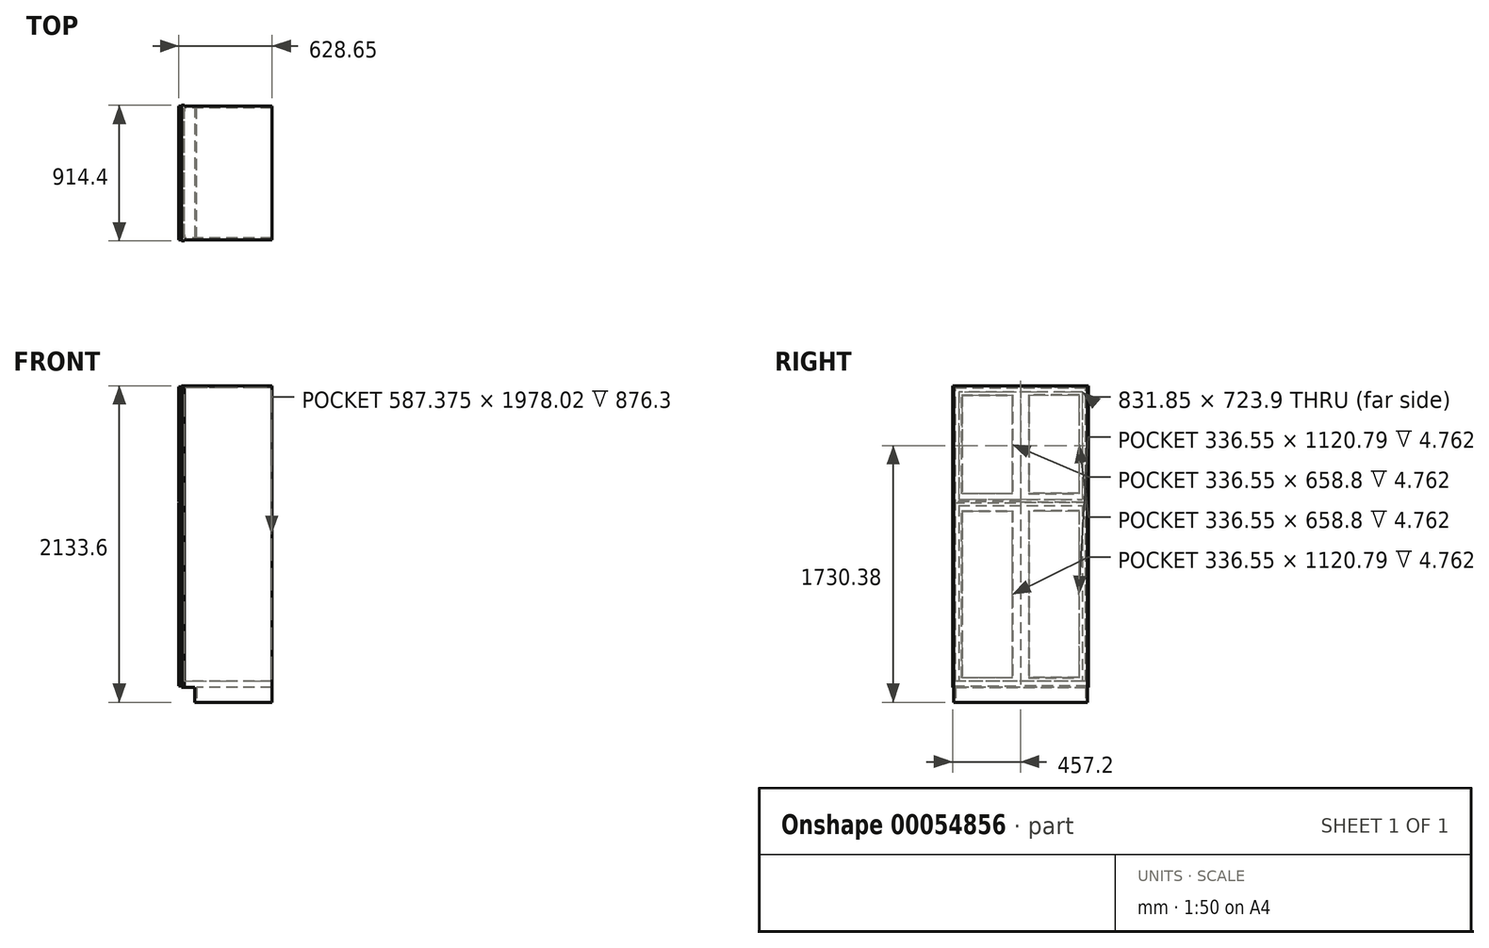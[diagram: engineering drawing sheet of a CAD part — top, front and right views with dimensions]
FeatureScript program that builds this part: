
annotation { "Feature Type Name" : "Feature", "Feature Type Description" : "" }
export const myFeature = defineFeature(function(context is Context, id is Id, definition is map)
    precondition{}
    {
        {
            var Q0;
            Q0=qCreatedBy(makeId("Front.planeOp"),FACE);
            var sketch = newSketch(context, id + "F0", { "sketchPlane" : qUnion([Q0])});
            skLineSegment(sketch, "E0.bottom", {"start": v(-304.8, -1066.8) * mm, "end": v(304.8, -1066.8) * mm});
            skLineSegment(sketch, "E0.top", {"start": v(-304.8, 1066.8) * mm, "end": v(304.8, 1066.8) * mm});
            skLineSegment(sketch, "E0.left", {"start": v(-304.8, -1066.8) * mm, "end": v(-304.8, 1066.8) * mm});
            skLineSegment(sketch, "E0.right", {"start": v(304.8, -1066.8) * mm, "end": v(304.8, 1066.8) * mm});
            skLineSegment(sketch, "E1", {"start": v(-304.8, -1066.8) * mm, "end": v(304.8, 1066.8) * mm, "construction": true});
            skSolve(sketch);
        }
        {
            var Q0;
            Q0=qSketchRegion(id+"F0",true);
            extrude(context, id + "F1", {"entities" : qUnion([Q0]), "oppositeDirection" : true, "depth" : 914.4 * mm});
        }
        {
            var Q0;
            Q0=makeQuery(id+"F1.opExtrude","CAP_FACE",FACE,{"disambiguationData":[OSD([sQuery(id+"F0.wireOp",EDGE,"E0.bottom"),sQuery(id+"F0.wireOp",EDGE,"E0.top"),sQuery(id+"F0.wireOp",EDGE,"E0.left"),sQuery(id+"F0.wireOp",EDGE,"E0.right")])],"isStart":true});
            var sketch = newSketch(context, id + "F2", { "sketchPlane" : qUnion([Q0])});
            skLineSegment(sketch, "E2.bottom", {"start": v(-304.8, -1066.8) * mm, "end": v(-215.9, -1066.8) * mm});
            skLineSegment(sketch, "E2.top", {"start": v(-304.8, -965.2) * mm, "end": v(-215.9, -965.2) * mm});
            skLineSegment(sketch, "E2.left", {"start": v(-304.8, -1066.8) * mm, "end": v(-304.8, -965.2) * mm});
            skLineSegment(sketch, "E2.right", {"start": v(-215.9, -1066.8) * mm, "end": v(-215.9, -965.2) * mm});
            skSolve(sketch);
        }
        {
            var Q0;
            Q0=qSketchRegion(id+"F2",true);
            extrude(context, id + "F3", {"entities" : qUnion([Q0]), "operationType" : NewBodyOperationType.REMOVE, "endBound" : BoundingType.THROUGH_ALL, "oppositeDirection" : true, "depth" : 25.4 * mm});
        }
        {
            var Q0;
            Q0=makeQuery(id+"F1.opExtrude","SWEPT_FACE",FACE,{"disambiguationData":[OSD([sQuery(id+"F0.wireOp",EDGE,"E0.left")])]});
            var sketch = newSketch(context, id + "F4", { "sketchPlane" : qUnion([Q0])});
            skLineSegment(sketch, "E3.bottom", {"start": v(-873.13, 1025.53) * mm, "end": v(-41.28, 1025.53) * mm});
            skLineSegment(sketch, "E3.top", {"start": v(-873.12, -923.93) * mm, "end": v(-41.27, -923.93) * mm});
            skLineSegment(sketch, "E3.left", {"start": v(-873.13, 1025.53) * mm, "end": v(-873.12, -923.93) * mm});
            skLineSegment(sketch, "E3.right", {"start": v(-41.28, 1025.53) * mm, "end": v(-41.27, -923.93) * mm});
            skSolve(sketch);
        }
        {
            var Q0;
            Q0=qSketchRegion(id+"F4",true);
            extrude(context, id + "F5", {"entities" : qUnion([Q0]), "operationType" : NewBodyOperationType.REMOVE, "oppositeDirection" : true, "depth" : 19.05 * mm});
        }
        {
            var Q0;
            Q0=makeQuery(id+"F1.opExtrude","SWEPT_FACE",FACE,{"disambiguationData":[OSD([sQuery(id+"F0.wireOp",EDGE,"E0.top")])]});
            var sketch = newSketch(context, id + "F6", { "sketchPlane" : qUnion([Q0])});
            skLineSegment(sketch, "E4.bottom", {"start": v(304.8, 914.4) * mm, "end": v(-285.75, 914.4) * mm});
            skLineSegment(sketch, "E4.top", {"start": v(304.8, 908.05) * mm, "end": v(-285.75, 908.05) * mm});
            skLineSegment(sketch, "E4.left", {"start": v(304.8, 914.4) * mm, "end": v(304.8, 908.05) * mm});
            skLineSegment(sketch, "E4.right", {"start": v(-285.75, 914.4) * mm, "end": v(-285.75, 908.05) * mm});
            skLineSegment(sketch, "E5.bottom", {"start": v(304.8, 0) * mm, "end": v(-285.75, 0) * mm});
            skLineSegment(sketch, "E5.top", {"start": v(304.8, 6.35) * mm, "end": v(-285.75, 6.35) * mm});
            skLineSegment(sketch, "E5.left", {"start": v(304.8, 0) * mm, "end": v(304.8, 6.35) * mm});
            skLineSegment(sketch, "E5.right", {"start": v(-285.75, 0) * mm, "end": v(-285.75, 6.35) * mm});
            skSolve(sketch);
        }
        {
            var Q0;
            Q0=qSketchRegion(id+"F6",true);
            extrude(context, id + "F7", {"entities" : qUnion([Q0]), "operationType" : NewBodyOperationType.REMOVE, "endBound" : BoundingType.THROUGH_ALL, "oppositeDirection" : true, "depth" : 25.4 * mm});
        }
        {
            var Q0;
            Q0=makeQuery(id+"F1.opExtrude","SWEPT_FACE",FACE,{"disambiguationData":[OSD([sQuery(id+"F0.wireOp",EDGE,"E0.top")])]});
            var sketch = newSketch(context, id + "F8", { "sketchPlane" : qUnion([Q0])});
            skLineSegment(sketch, "E6.bottom", {"start": v(301.63, 895.35) * mm, "end": v(-285.75, 895.35) * mm});
            skLineSegment(sketch, "E6.top", {"start": v(301.63, 19.05) * mm, "end": v(-285.75, 19.05) * mm});
            skLineSegment(sketch, "E6.left", {"start": v(301.62, 895.35) * mm, "end": v(301.63, 19.05) * mm});
            skLineSegment(sketch, "E6.right", {"start": v(-285.75, 895.35) * mm, "end": v(-285.75, 19.05) * mm});
            skSolve(sketch);
        }
        {
            var Q0;
            Q0=qSketchRegion(id+"F8",true);
            var Q1;
            Q1=makeQuery(id+"F5.boolean.opBoolean","COPY",FACE,{"derivedFrom":makeQuery(id+"F5.opExtrude","SWEPT_FACE",FACE,{"disambiguationData":[OSD([sQuery(id+"F4.wireOp",EDGE,"E3.top")])]})});
            extrude(context, id + "F9", {"entities" : qUnion([Q0]), "operationType" : NewBodyOperationType.REMOVE, "endBound" : BoundingType.UP_TO_SURFACE, "oppositeDirection" : true, "endBoundEntityFace" : qUnion([Q1]), "depth" : 25.4 * mm});
        }
        {
            var Q0;
            Q0=makeQuery(id+"F1.opExtrude","SWEPT_FACE",FACE,{"disambiguationData":[OSD([sQuery(id+"F0.wireOp",EDGE,"E0.left")])]});
            var sketch = newSketch(context, id + "F10", { "sketchPlane" : qUnion([Q0])});
            skLineSegment(sketch, "E7.bottom", {"start": v(-873.13, 301.63) * mm, "end": v(-41.28, 301.63) * mm});
            skLineSegment(sketch, "E7.top", {"start": v(-873.13, 260.35) * mm, "end": v(-41.28, 260.35) * mm});
            skLineSegment(sketch, "E7.left", {"start": v(-873.13, 301.63) * mm, "end": v(-873.13, 260.35) * mm});
            skLineSegment(sketch, "E7.right", {"start": v(-41.28, 301.63) * mm, "end": v(-41.28, 260.35) * mm});
            skSolve(sketch);
        }
        {
            var Q0;
            Q0=qSketchRegion(id+"F10",true);
            var Q1;
            Q1=makeQuery(id+"F9.boolean.opBoolean","COPY",FACE,{"derivedFrom":makeQuery(id+"F9.opExtrude","SWEPT_FACE",FACE,{"disambiguationData":[OSD([sQuery(id+"F8.wireOp",EDGE,"E6.right")])]})});
            extrude(context, id + "F11", {"entities" : qUnion([Q0]), "operationType" : NewBodyOperationType.ADD, "endBound" : BoundingType.UP_TO_SURFACE, "oppositeDirection" : true, "endBoundEntityFace" : qUnion([Q1]), "depth" : 25.4 * mm});
        }
        {
            var Q0;
            Q0=makeQuery(id+"F11.boolean.opBoolean","MERGE",FACE,{"derivedFrom":[makeQuery(id+"F1.opExtrude","SWEPT_FACE",FACE,{"disambiguationData":[OSD([sQuery(id+"F0.wireOp",EDGE,"E0.left")])]}),makeQuery(id+"F11.opExtrude","CAP_FACE",FACE,{"disambiguationData":[OSD([sQuery(id+"F10.wireOp",EDGE,"E7.bottom"),sQuery(id+"F10.wireOp",EDGE,"E7.top"),sQuery(id+"F10.wireOp",EDGE,"E7.left"),sQuery(id+"F10.wireOp",EDGE,"E7.right")])],"isStart":true})]});
            var sketch = newSketch(context, id + "F12", { "sketchPlane" : qUnion([Q0])});
            skLineSegment(sketch, "E8.bottom", {"start": v(-908.05, 277.83) * mm, "end": v(-457.2, 277.83) * mm});
            skLineSegment(sketch, "E8.top", {"start": v(-908.05, -957.26) * mm, "end": v(-457.2, -957.26) * mm});
            skLineSegment(sketch, "E8.left", {"start": v(-908.05, 277.83) * mm, "end": v(-908.05, -957.26) * mm});
            skLineSegment(sketch, "E8.right", {"start": v(-457.2, 277.83) * mm, "end": v(-457.2, -957.26) * mm});
            skLineSegment(sketch, "E9.bottom", {"start": v(-850.9, 220.68) * mm, "end": v(-514.35, 220.68) * mm});
            skLineSegment(sketch, "E9.top", {"start": v(-850.9, -900.11) * mm, "end": v(-514.35, -900.11) * mm});
            skLineSegment(sketch, "E9.left", {"start": v(-850.9, 220.68) * mm, "end": v(-850.9, -900.11) * mm});
            skLineSegment(sketch, "E9.right", {"start": v(-514.35, 220.68) * mm, "end": v(-514.35, -900.11) * mm});
            skLineSegment(sketch, "E10", {"start": v(-457.2, 260.35) * mm, "end": v(-457.2, -923.93) * mm, "construction": true});
            skLineSegment(sketch, "E11.bottom", {"start": v(-457.2, 1058.86) * mm, "end": v(-908.05, 1058.86) * mm});
            skLineSegment(sketch, "E11.top", {"start": v(-457.2, 285.76) * mm, "end": v(-908.05, 285.76) * mm});
            skLineSegment(sketch, "E11.left", {"start": v(-457.2, 1058.86) * mm, "end": v(-457.2, 285.76) * mm});
            skLineSegment(sketch, "E11.right", {"start": v(-908.05, 1058.86) * mm, "end": v(-908.05, 285.76) * mm});
            skLineSegment(sketch, "E12.bottom", {"start": v(-850.9, 1001.71) * mm, "end": v(-514.35, 1001.71) * mm});
            skLineSegment(sketch, "E12.top", {"start": v(-850.9, 342.91) * mm, "end": v(-514.35, 342.91) * mm});
            skLineSegment(sketch, "E12.left", {"start": v(-850.9, 1001.71) * mm, "end": v(-850.9, 342.91) * mm});
            skLineSegment(sketch, "E12.right", {"start": v(-514.35, 1001.71) * mm, "end": v(-514.35, 342.91) * mm});
            skSolve(sketch);
        }
        {
            var Q0;
            Q0=qSketchRegion(id+"F12",true);
            extrude(context, id + "F13", {"entities" : qUnion([Q0]), "depth" : 19.05 * mm});
        }
        {
            var Q0;
            Q0=makeQuery(id+"F13.opExtrude","SWEPT_FACE",FACE,{"disambiguationData":[OSD([sQuery(id+"F12.wireOp",EDGE,"E9.top")])]});
            var sketch = newSketch(context, id + "F14", { "sketchPlane" : qUnion([Q0])});
            skLineSegment(sketch, "E13.bottom", {"start": v(-315.91, 850.9) * mm, "end": v(-309.56, 850.9) * mm});
            skLineSegment(sketch, "E13.top", {"start": v(-315.91, 514.35) * mm, "end": v(-309.56, 514.35) * mm});
            skLineSegment(sketch, "E13.left", {"start": v(-315.91, 850.9) * mm, "end": v(-315.91, 514.35) * mm});
            skLineSegment(sketch, "E13.right", {"start": v(-309.56, 850.9) * mm, "end": v(-309.56, 514.35) * mm});
            skSolve(sketch);
        }
        {
            var Q0;
            Q0=qSketchRegion(id+"F14",true);
            extrude(context, id + "F15", {"entities" : qUnion([Q0]), "operationType" : NewBodyOperationType.ADD, "endBound" : BoundingType.UP_TO_NEXT, "depth" : 25.4 * mm});
        }
        {
            var Q0;
            Q0=makeQuery(id+"F13.opExtrude","SWEPT_FACE",FACE,{"disambiguationData":[OSD([sQuery(id+"F12.wireOp",EDGE,"E12.top")])]});
            var sketch = newSketch(context, id + "F16", { "sketchPlane" : qUnion([Q0])});
            skLineSegment(sketch, "E14.bottom", {"start": v(-309.56, 850.9) * mm, "end": v(-315.91, 850.9) * mm});
            skLineSegment(sketch, "E14.top", {"start": v(-309.56, 514.35) * mm, "end": v(-315.91, 514.35) * mm});
            skLineSegment(sketch, "E14.left", {"start": v(-309.56, 850.9) * mm, "end": v(-309.56, 514.35) * mm});
            skLineSegment(sketch, "E14.right", {"start": v(-315.91, 850.9) * mm, "end": v(-315.91, 514.35) * mm});
            skSolve(sketch);
        }
        {
            var Q0;
            Q0=qSketchRegion(id+"F16",true);
            extrude(context, id + "F17", {"entities" : qUnion([Q0]), "operationType" : NewBodyOperationType.ADD, "endBound" : BoundingType.UP_TO_NEXT, "depth" : 25.4 * mm});
        }
        {
            var Q0;
            Q0=makeQuery(id+"F13.opExtrude","CAP_EDGE",EDGE,{"disambiguationData":[OSD([sQuery(id+"F12.wireOp",EDGE,"E9.left")])],"isStart":false});
            var Q1;
            Q1=makeQuery(id+"F13.opExtrude","CAP_EDGE",EDGE,{"disambiguationData":[OSD([sQuery(id+"F12.wireOp",EDGE,"E9.top")])],"isStart":false});
            var Q2;
            Q2=makeQuery(id+"F13.opExtrude","CAP_EDGE",EDGE,{"disambiguationData":[OSD([sQuery(id+"F12.wireOp",EDGE,"E9.right")])],"isStart":false});
            var Q3;
            Q3=makeQuery(id+"F13.opExtrude","CAP_EDGE",EDGE,{"disambiguationData":[OSD([sQuery(id+"F12.wireOp",EDGE,"E9.bottom")])],"isStart":false});
            var Q4;
            Q4=makeQuery(id+"F13.opExtrude","CAP_EDGE",EDGE,{"disambiguationData":[OSD([sQuery(id+"F12.wireOp",EDGE,"E12.top")])],"isStart":false});
            var Q5;
            Q5=makeQuery(id+"F13.opExtrude","CAP_EDGE",EDGE,{"disambiguationData":[OSD([sQuery(id+"F12.wireOp",EDGE,"E12.left")])],"isStart":false});
            var Q6;
            Q6=makeQuery(id+"F13.opExtrude","CAP_EDGE",EDGE,{"disambiguationData":[OSD([sQuery(id+"F12.wireOp",EDGE,"E12.right")])],"isStart":false});
            var Q7;
            Q7=makeQuery(id+"F13.opExtrude","CAP_EDGE",EDGE,{"disambiguationData":[OSD([sQuery(id+"F12.wireOp",EDGE,"E12.bottom")])],"isStart":false});
            chamfer(context, id + "F18", {"entities" : qUnion([Q0, Q1, Q2, Q3, Q4, Q5, Q6, Q7]), "width" : 3.17 * mm, "tangentPropagation" : true});
        }
        {
            var Q0;
            Q0=makeQuery(id+"F13.opExtrude","SWEPT_BODY",BODY,{"disambiguationData":[OSD([sQuery(id+"F12.wireOp",EDGE,"E8.bottom"),sQuery(id+"F12.wireOp",EDGE,"E8.top"),sQuery(id+"F12.wireOp",EDGE,"E8.left"),sQuery(id+"F12.wireOp",EDGE,"E8.right"),sQuery(id+"F12.wireOp",EDGE,"E9.bottom"),sQuery(id+"F12.wireOp",EDGE,"E9.top"),sQuery(id+"F12.wireOp",EDGE,"E9.left"),sQuery(id+"F12.wireOp",EDGE,"E9.right")])]});
            var Q1;
            Q1=makeQuery(id+"F13.opExtrude","SWEPT_BODY",BODY,{"disambiguationData":[OSD([sQuery(id+"F12.wireOp",EDGE,"E11.bottom"),sQuery(id+"F12.wireOp",EDGE,"E11.top"),sQuery(id+"F12.wireOp",EDGE,"E11.left"),sQuery(id+"F12.wireOp",EDGE,"E11.right"),sQuery(id+"F12.wireOp",EDGE,"E12.bottom"),sQuery(id+"F12.wireOp",EDGE,"E12.top"),sQuery(id+"F12.wireOp",EDGE,"E12.left"),sQuery(id+"F12.wireOp",EDGE,"E12.right")])]});
            var Q2;
            Q2=makeQuery(id+"F13.opExtrude","SWEPT_FACE",FACE,{"disambiguationData":[OSD([sQuery(id+"F12.wireOp",EDGE,"E8.right")])]});
            mirror(context, id + "F19", {"entities" : qUnion([Q0, Q1]), "mirrorPlane" : qUnion([Q2])});
        }
        {
            var Q0;
            Q0=makeQuery(id+"F1.opExtrude","SWEPT_FACE",FACE,{"disambiguationData":[OSD([sQuery(id+"F0.wireOp",EDGE,"E0.bottom")])]});
            var sketch = newSketch(context, id + "F20", { "sketchPlane" : qUnion([Q0])});
            skLineSegment(sketch, "E15.bottom", {"start": v(301.63, -19.05) * mm, "end": v(-203.2, -19.05) * mm});
            skLineSegment(sketch, "E15.top", {"start": v(301.63, -895.35) * mm, "end": v(-203.2, -895.35) * mm});
            skLineSegment(sketch, "E15.left", {"start": v(301.63, -19.05) * mm, "end": v(301.63, -895.35) * mm});
            skLineSegment(sketch, "E15.right", {"start": v(-203.2, -19.05) * mm, "end": v(-203.2, -895.35) * mm});
            skSolve(sketch);
        }
        {
            var Q0;
            Q0=qSketchRegion(id+"F20",true);
            extrude(context, id + "F21", {"entities" : qUnion([Q0]), "operationType" : NewBodyOperationType.REMOVE, "oppositeDirection" : true, "depth" : 101.6 * mm});
        }
        {
            var Q0;
            Q0=makeQuery(id+"F11.boolean.opBoolean","MERGE",FACE,{"derivedFrom":[makeQuery(id+"F9.boolean.opBoolean","COPY",FACE,{"derivedFrom":makeQuery(id+"F9.opExtrude","SWEPT_FACE",FACE,{"disambiguationData":[OSD([sQuery(id+"F8.wireOp",EDGE,"E6.right")])]})}),makeQuery(id+"F11.opExtrude","CAP_FACE",FACE,{"disambiguationData":[OSD([sQuery(id+"F10.wireOp",EDGE,"E7.bottom"),sQuery(id+"F10.wireOp",EDGE,"E7.top"),sQuery(id+"F10.wireOp",EDGE,"E7.left"),sQuery(id+"F10.wireOp",EDGE,"E7.right")])],"isStart":false})]});
            var sketch = newSketch(context, id + "F22", { "sketchPlane" : qUnion([Q0])});
            skLineSegment(sketch, "E16.bottom", {"start": v(19.05, 1066.8) * mm, "end": v(895.35, 1066.8) * mm});
            skLineSegment(sketch, "E16.top", {"start": v(19.05, 1054.1) * mm, "end": v(895.35, 1054.1) * mm});
            skLineSegment(sketch, "E16.left", {"start": v(19.05, 1066.8) * mm, "end": v(19.05, 1054.1) * mm});
            skLineSegment(sketch, "E16.right", {"start": v(895.35, 1066.8) * mm, "end": v(895.35, 1054.1) * mm});
            skSolve(sketch);
        }
        {
            var Q0;
            Q0=makeQuery(id+"F22.imprint","IMPRINT",FACE,{"disambiguationData":[TD([[makeQuery(id+"F22.imprint","IMPRINT",EDGE,{"derivedFrom":sQuery(id+"F22.wireOp",EDGE,"E16.bottom")}),1.0]])]});
            extrude(context, id + "F23", {"entities" : qUnion([Q0]), "operationType" : NewBodyOperationType.ADD, "endBound" : BoundingType.UP_TO_NEXT, "depth" : 25.4 * mm});
        }
    });
